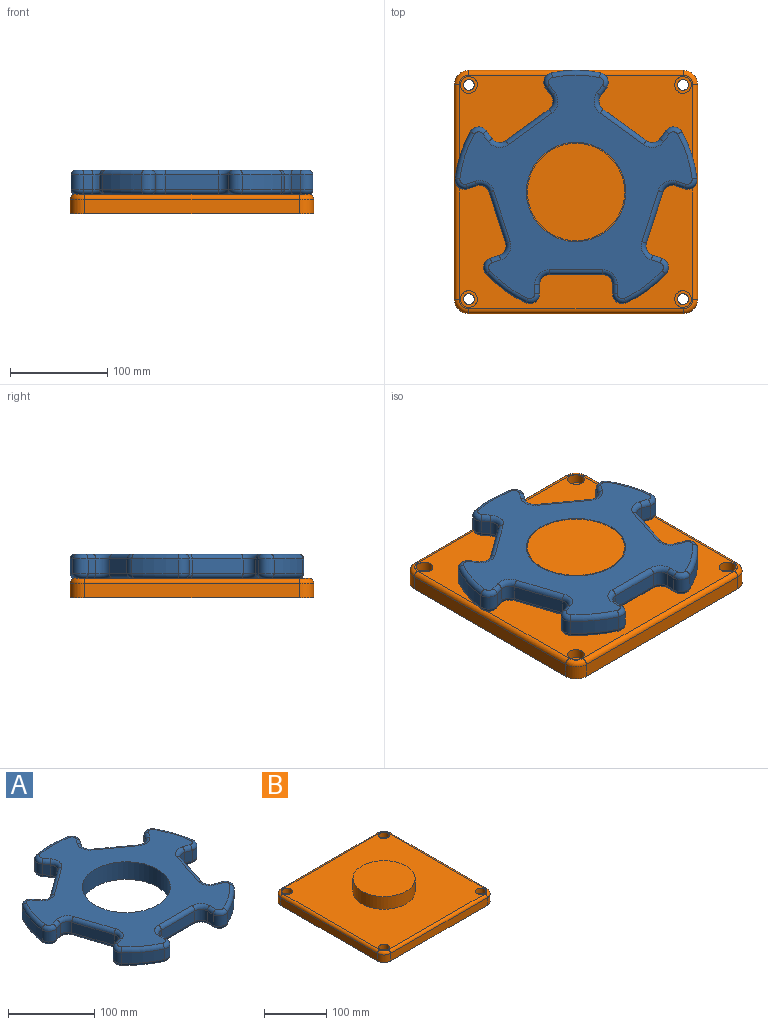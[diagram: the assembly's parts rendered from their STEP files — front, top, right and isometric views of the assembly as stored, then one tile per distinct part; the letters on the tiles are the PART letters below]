
ASSEMBLY  parts=2 mates=1
PART A: 123 faces, bbox 268.9x258.5x25 mm
  f0: plane 238.57x229.73mm, normal (0,0,1), area 21505.7mm2, adj f6,f83,f84,f85,f86,f87,f88,f89
  f1: plane 238.57x229.73mm, normal (0,0,-1), area 21505.7mm2, adj f6,f43,f44,f45,f46,f47,f48,f49
  f2: cylinder r=125mm len=47.82mm, axis (0,0,-1), area 759.5mm2, adj f34,f42,f74,f114
  f3: cylinder r=125mm len=50.29mm, axis (0,0,-1), area 759.5mm2, adj f27,f35,f75,f115
  f4: cylinder r=125mm len=47.82mm, axis (0,0,-1), area 759.5mm2, adj f20,f28,f59,f99
  f5: cylinder r=125mm len=40.68mm, axis (0,0,-1), area 759.5mm2, adj f13,f21,f43,f83
  f6: cylinder r=51mm len=102mm, axis (0,0,-1), area 8011.1mm2, adj f0,f1
  f7: cylinder r=125mm len=40.68mm, axis (0,0,-1), area 759.5mm2, adj f14,f41,f58,f98
  f8: plane 15x9.73mm, normal (-1,0,0), area 146mm2, adj f11,f14,f54,f94
  f9: plane 55x15mm, normal (0,-1,0), area 825mm2, adj f11,f12,f50,f90
  f10: plane 15x9.73mm, normal (1,0,0), area 146mm2, adj f12,f13,f46,f86
  f11: cylinder r=10mm len=15mm, axis (0,0,-1), area 235.6mm2, adj f8,f9,f52,f92
  f12: cylinder r=10mm len=15mm, axis (0,0,-1), area 235.6mm2, adj f9,f10,f48,f88
  f13: cylinder r=10mm len=15mm, axis (0,0,-1), area 299.5mm2, adj f5,f10,f44,f84
  f14: cylinder r=10mm len=15mm, axis (0,0,-1), area 299.5mm2, adj f7,f8,f56,f96
  f15: plane 15x9.26mm, normal (-0.31,0.95,0), area 146mm2, adj f18,f21,f47,f87
  f16: plane 52.31x17mm, normal (-0.95,-0.31,0), area 825mm2, adj f18,f19,f51,f91
  f17: plane 15x9.26mm, normal (0.31,-0.95,0), area 146mm2, adj f19,f20,f55,f95
  f18: cylinder r=10mm len=15mm, axis (0,0,-1), area 235.6mm2, adj f15,f16,f49,f89
  f19: cylinder r=10mm len=15mm, axis (0,0,-1), area 235.6mm2, adj f16,f17,f53,f93
  f20: cylinder r=10mm len=15mm, axis (0,0,-1), area 299.5mm2, adj f4,f17,f57,f97
  f21: cylinder r=10mm len=16.25mm, axis (0,0,-1), area 299.5mm2, adj f5,f15,f45,f85
  f22: plane 15x7.87mm, normal (0.81,0.59,0), area 146mm2, adj f25,f28,f63,f103
  f23: plane 44.5x32.33mm, normal (-0.59,0.81,0), area 825mm2, adj f25,f26,f67,f107
  f24: plane 15x7.87mm, normal (-0.81,-0.59,0), area 146mm2, adj f26,f27,f71,f111
  f25: cylinder r=10mm len=15mm, axis (0,0,-1), area 235.6mm2, adj f22,f23,f65,f105
  f26: cylinder r=10mm len=15mm, axis (0,0,-1), area 235.6mm2, adj f23,f24,f69,f109
  f27: cylinder r=10mm len=15.67mm, axis (0,0,-1), area 299.5mm2, adj f3,f24,f73,f113
  f28: cylinder r=10mm len=16.78mm, axis (0,0,-1), area 299.5mm2, adj f4,f22,f61,f101
  f29: plane 15x7.87mm, normal (0.81,-0.59,0), area 146mm2, adj f32,f35,f79,f119
  f30: plane 44.5x32.33mm, normal (0.59,0.81,0), area 825mm2, adj f32,f33,f82,f122
  f31: plane 15x7.87mm, normal (-0.81,0.59,0), area 146mm2, adj f33,f34,f78,f118
  f32: cylinder r=10mm len=15mm, axis (0,0,-1), area 235.6mm2, adj f29,f30,f81,f121
  f33: cylinder r=10mm len=15mm, axis (0,0,-1), area 235.6mm2, adj f30,f31,f80,f120
  f34: cylinder r=10mm len=16.78mm, axis (0,0,-1), area 299.5mm2, adj f2,f31,f76,f116
  f35: cylinder r=10mm len=15.67mm, axis (0,0,-1), area 299.5mm2, adj f3,f29,f77,f117
  f36: plane 15x9.26mm, normal (-0.31,-0.95,0), area 146mm2, adj f39,f42,f70,f110
  f37: plane 52.31x17mm, normal (0.95,-0.31,0), area 825mm2, adj f39,f40,f66,f106
  f38: plane 15x9.26mm, normal (0.31,0.95,0), area 146mm2, adj f40,f41,f62,f102
  f39: cylinder r=10mm len=15mm, axis (0,0,-1), area 235.6mm2, adj f36,f37,f68,f108
  f40: cylinder r=10mm len=15mm, axis (0,0,-1), area 235.6mm2, adj f37,f38,f64,f104
  f41: cylinder r=10mm len=16.25mm, axis (0,0,-1), area 299.5mm2, adj f7,f38,f60,f100
  f42: cylinder r=10mm len=15mm, axis (0,0,-1), area 299.5mm2, adj f2,f36,f72,f112
  f43: torus R=120mm, axis (0,0,1), area 391.9mm2, adj f1,f5,f44,f45
  f44: torus R=5mm, axis (0,0,1), area 128.3mm2, adj f1,f13,f43,f46
  f45: torus R=5mm, axis (0,0,1), area 128.3mm2, adj f1,f21,f43,f47
  f46: cylinder r=5mm len=9.73mm, axis (0,-1,0), area 76.4mm2, adj f1,f10,f44,f48
  f47: cylinder r=5mm len=10.8mm, axis (0.95,0.31,0), area 76.4mm2, adj f1,f15,f45,f49
  f48: torus R=15mm, axis (0,0,1), area 145.8mm2, adj f1,f12,f46,f50
  f49: torus R=15mm, axis (0,0,1), area 145.8mm2, adj f1,f18,f47,f51
  f50: cylinder r=5mm len=55mm, axis (-1,0,0), area 432mm2, adj f1,f9,f48,f52
  f51: cylinder r=5mm len=53.85mm, axis (-0.31,0.95,0), area 432mm2, adj f1,f16,f49,f53
  f52: torus R=15mm, axis (0,0,1), area 145.8mm2, adj f1,f11,f50,f54
  f53: torus R=15mm, axis (0,0,1), area 145.8mm2, adj f1,f19,f51,f55
  f54: cylinder r=5mm len=9.73mm, axis (0,1,0), area 76.4mm2, adj f1,f8,f52,f56
  f55: cylinder r=5mm len=10.8mm, axis (-0.95,-0.31,0), area 76.4mm2, adj f1,f17,f53,f57
  f56: torus R=5mm, axis (0,0,1), area 128.3mm2, adj f1,f14,f54,f58
  f57: torus R=5mm, axis (0,0,1), area 128.3mm2, adj f1,f20,f55,f59
  f58: torus R=120mm, axis (0,0,1), area 391.9mm2, adj f1,f7,f56,f60
  f59: torus R=120mm, axis (0,0,1), area 391.9mm2, adj f1,f4,f57,f61
  f60: torus R=5mm, axis (0,0,1), area 128.3mm2, adj f1,f41,f58,f62
  f61: torus R=5mm, axis (0,0,1), area 128.3mm2, adj f1,f28,f59,f63
  f62: cylinder r=5mm len=10.8mm, axis (0.95,-0.31,0), area 76.4mm2, adj f1,f38,f60,f64
  f63: cylinder r=5mm len=10.81mm, axis (0.59,-0.81,0), area 76.4mm2, adj f1,f22,f61,f65
  f64: torus R=15mm, axis (0,0,1), area 145.8mm2, adj f1,f40,f62,f66
  f65: torus R=15mm, axis (0,0,1), area 145.8mm2, adj f1,f25,f63,f67
  f66: cylinder r=5mm len=53.85mm, axis (-0.31,-0.95,0), area 432mm2, adj f1,f37,f64,f68
  f67: cylinder r=5mm len=47.44mm, axis (0.81,0.59,0), area 432mm2, adj f1,f23,f65,f69
  f68: torus R=15mm, axis (0,0,1), area 145.8mm2, adj f1,f39,f66,f70
  f69: torus R=15mm, axis (0,0,1), area 145.8mm2, adj f1,f26,f67,f71
  f70: cylinder r=5mm len=10.8mm, axis (-0.95,0.31,0), area 76.4mm2, adj f1,f36,f68,f72
  f71: cylinder r=5mm len=10.81mm, axis (-0.59,0.81,0), area 76.4mm2, adj f1,f24,f69,f73
  f72: torus R=5mm, axis (0,0,1), area 128.3mm2, adj f1,f42,f70,f74
  f73: torus R=5mm, axis (0,0,1), area 128.3mm2, adj f1,f27,f71,f75
  f74: torus R=120mm, axis (0,0,1), area 391.9mm2, adj f1,f2,f72,f76
  f75: torus R=120mm, axis (0,0,1), area 391.9mm2, adj f1,f3,f73,f77
  f76: torus R=5mm, axis (0,0,1), area 128.3mm2, adj f1,f34,f74,f78
  f77: torus R=5mm, axis (0,0,1), area 128.3mm2, adj f1,f35,f75,f79
  f78: cylinder r=5mm len=10.81mm, axis (0.59,0.81,0), area 76.4mm2, adj f1,f31,f76,f80
  f79: cylinder r=5mm len=10.81mm, axis (-0.59,-0.81,0), area 76.4mm2, adj f1,f29,f77,f81
  f80: torus R=15mm, axis (0,0,1), area 145.8mm2, adj f1,f33,f78,f82
  f81: torus R=15mm, axis (0,0,1), area 145.8mm2, adj f1,f32,f79,f82
  f82: cylinder r=5mm len=47.44mm, axis (0.81,-0.59,0), area 432mm2, adj f1,f30,f80,f81
  f83: torus R=120mm, axis (0,0,1), area 391.9mm2, adj f0,f5,f84,f85
  f84: torus R=5mm, axis (0,0,1), area 128.3mm2, adj f0,f13,f83,f86
  f85: torus R=5mm, axis (0,0,1), area 128.3mm2, adj f0,f21,f83,f87
  f86: cylinder r=5mm len=9.73mm, axis (0,1,0), area 76.4mm2, adj f0,f10,f84,f88
  f87: cylinder r=5mm len=10.8mm, axis (-0.95,-0.31,0), area 76.4mm2, adj f0,f15,f85,f89
  f88: torus R=15mm, axis (0,0,1), area 145.8mm2, adj f0,f12,f86,f90
  f89: torus R=15mm, axis (0,0,1), area 145.8mm2, adj f0,f18,f87,f91
  f90: cylinder r=5mm len=55mm, axis (1,0,0), area 432mm2, adj f0,f9,f88,f92
  f91: cylinder r=5mm len=53.85mm, axis (0.31,-0.95,0), area 432mm2, adj f0,f16,f89,f93
  f92: torus R=15mm, axis (0,0,1), area 145.8mm2, adj f0,f11,f90,f94
  f93: torus R=15mm, axis (0,0,1), area 145.8mm2, adj f0,f19,f91,f95
  f94: cylinder r=5mm len=9.73mm, axis (0,-1,0), area 76.4mm2, adj f0,f8,f92,f96
  f95: cylinder r=5mm len=10.8mm, axis (0.95,0.31,0), area 76.4mm2, adj f0,f17,f93,f97
  f96: torus R=5mm, axis (0,0,1), area 128.3mm2, adj f0,f14,f94,f98
  f97: torus R=5mm, axis (0,0,1), area 128.3mm2, adj f0,f20,f95,f99
  f98: torus R=120mm, axis (0,0,1), area 391.9mm2, adj f0,f7,f96,f100
  f99: torus R=120mm, axis (0,0,1), area 391.9mm2, adj f0,f4,f97,f101
  f100: torus R=5mm, axis (0,0,1), area 128.3mm2, adj f0,f41,f98,f102
  f101: torus R=5mm, axis (0,0,1), area 128.3mm2, adj f0,f28,f99,f103
  f102: cylinder r=5mm len=10.8mm, axis (-0.95,0.31,0), area 76.4mm2, adj f0,f38,f100,f104
  f103: cylinder r=5mm len=10.81mm, axis (-0.59,0.81,0), area 76.4mm2, adj f0,f22,f101,f105
  f104: torus R=15mm, axis (0,0,1), area 145.8mm2, adj f0,f40,f102,f106
  f105: torus R=15mm, axis (0,0,1), area 145.8mm2, adj f0,f25,f103,f107
  f106: cylinder r=5mm len=53.85mm, axis (0.31,0.95,0), area 432mm2, adj f0,f37,f104,f108
  f107: cylinder r=5mm len=47.44mm, axis (-0.81,-0.59,0), area 432mm2, adj f0,f23,f105,f109
  f108: torus R=15mm, axis (0,0,1), area 145.8mm2, adj f0,f39,f106,f110
  f109: torus R=15mm, axis (0,0,1), area 145.8mm2, adj f0,f26,f107,f111
  f110: cylinder r=5mm len=10.8mm, axis (0.95,-0.31,0), area 76.4mm2, adj f0,f36,f108,f112
  f111: cylinder r=5mm len=10.81mm, axis (0.59,-0.81,0), area 76.4mm2, adj f0,f24,f109,f113
  f112: torus R=5mm, axis (0,0,1), area 128.3mm2, adj f0,f42,f110,f114
  f113: torus R=5mm, axis (0,0,1), area 128.3mm2, adj f0,f27,f111,f115
  f114: torus R=120mm, axis (0,0,1), area 391.9mm2, adj f0,f2,f112,f116
  f115: torus R=120mm, axis (0,0,1), area 391.9mm2, adj f0,f3,f113,f117
  f116: torus R=5mm, axis (0,0,1), area 128.3mm2, adj f0,f34,f114,f118
  f117: torus R=5mm, axis (0,0,1), area 128.3mm2, adj f0,f35,f115,f119
  f118: cylinder r=5mm len=10.81mm, axis (-0.59,-0.81,0), area 76.4mm2, adj f0,f31,f116,f120
  f119: cylinder r=5mm len=10.81mm, axis (0.59,0.81,0), area 76.4mm2, adj f0,f29,f117,f121
  f120: torus R=15mm, axis (0,0,1), area 145.8mm2, adj f0,f33,f118,f122
  f121: torus R=15mm, axis (0,0,1), area 145.8mm2, adj f0,f32,f119,f122
  f122: cylinder r=5mm len=47.44mm, axis (-0.81,0.59,0), area 432mm2, adj f0,f30,f120,f121
PART B: 32 faces, bbox 252.5x252.5x45 mm
  f0: plane 220x15mm, normal (1,0,0), area 3300mm2, adj f5,f8,f11,f27
  f1: plane 220x15mm, normal (0,1,0), area 3300mm2, adj f5,f8,f9,f31
  f2: plane 220x15mm, normal (-1,0,0), area 3300mm2, adj f5,f9,f10,f28
  f3: plane 220x15mm, normal (0,-1,0), area 3300mm2, adj f5,f10,f11,f24
  f4: plane 240x240mm, normal (0,0,1), area 48725.4mm2, adj f6,f14,f17,f20,f23,f24,f25,f26
  f5: plane 250x250mm, normal (0,0,-1), area 61926.7mm2, adj f0,f1,f2,f3,f8,f9,f10,f11
  f6: cylinder r=50mm len=100mm, axis (0,0,-1), area 7854mm2, adj f4,f7
  f7: plane 100x100mm, normal (0,0,1), area 7854mm2, adj f6
  f8: cylinder r=15mm len=15mm, axis (0,0,-1), area 353.4mm2, adj f0,f1,f5,f29
  f9: cylinder r=15mm len=15mm, axis (0,0,1), area 353.4mm2, adj f1,f2,f5,f30
  f10: cylinder r=15mm len=15mm, axis (0,0,-1), area 353.4mm2, adj f2,f3,f5,f26
  f11: cylinder r=15mm len=15mm, axis (0,0,1), area 353.4mm2, adj f0,f3,f5,f25
  f12: cylinder r=5.5mm len=11mm, axis (0,0,1), area 345.6mm2, adj f5,f13
  f13: plane 17.25x17.25mm, normal (0,0,1), area 138.7mm2, adj f12,f14
  f14: cylinder r=8.62mm len=17.25mm, axis (0,0,1), area 541.9mm2, adj f4,f13
  f15: cylinder r=5.5mm len=11mm, axis (0,0,1), area 345.6mm2, adj f5,f16
  f16: plane 17.25x17.25mm, normal (0,0,1), area 138.7mm2, adj f15,f17
  f17: cylinder r=8.62mm len=17.25mm, axis (0,0,1), area 541.9mm2, adj f4,f16
  f18: cylinder r=5.5mm len=11mm, axis (0,0,1), area 345.6mm2, adj f5,f19
  f19: plane 17.25x17.25mm, normal (0,0,1), area 138.7mm2, adj f18,f20
  f20: cylinder r=8.62mm len=17.25mm, axis (0,0,1), area 541.9mm2, adj f4,f19
  f21: cylinder r=5.5mm len=11mm, axis (0,0,1), area 345.6mm2, adj f5,f22
  f22: plane 17.25x17.25mm, normal (0,0,1), area 138.7mm2, adj f21,f23
  f23: cylinder r=8.62mm len=17.25mm, axis (0,0,1), area 541.9mm2, adj f4,f22
  f24: cylinder r=5mm len=220mm, axis (-1,0,0), area 1727.9mm2, adj f3,f4,f25,f26
  f25: torus R=10mm, axis (0,0,1), area 162.6mm2, adj f4,f11,f24,f27
  f26: torus R=10mm, axis (0,0,1), area 162.6mm2, adj f4,f10,f24,f28
  f27: cylinder r=5mm len=220mm, axis (0,-1,0), area 1727.9mm2, adj f0,f4,f25,f29
  f28: cylinder r=5mm len=220mm, axis (0,1,0), area 1727.9mm2, adj f2,f4,f26,f30
  f29: torus R=10mm, axis (0,0,1), area 162.6mm2, adj f4,f8,f27,f31
  f30: torus R=10mm, axis (0,0,1), area 162.6mm2, adj f4,f9,f28,f31
  f31: cylinder r=5mm len=220mm, axis (1,0,0), area 1727.9mm2, adj f1,f4,f29,f30
PLACE A at identity
PLACE B at identity fixed
MATE revolute B.f6 <-> A.f2  axis (0,0,1) through (0,0,45)mm
